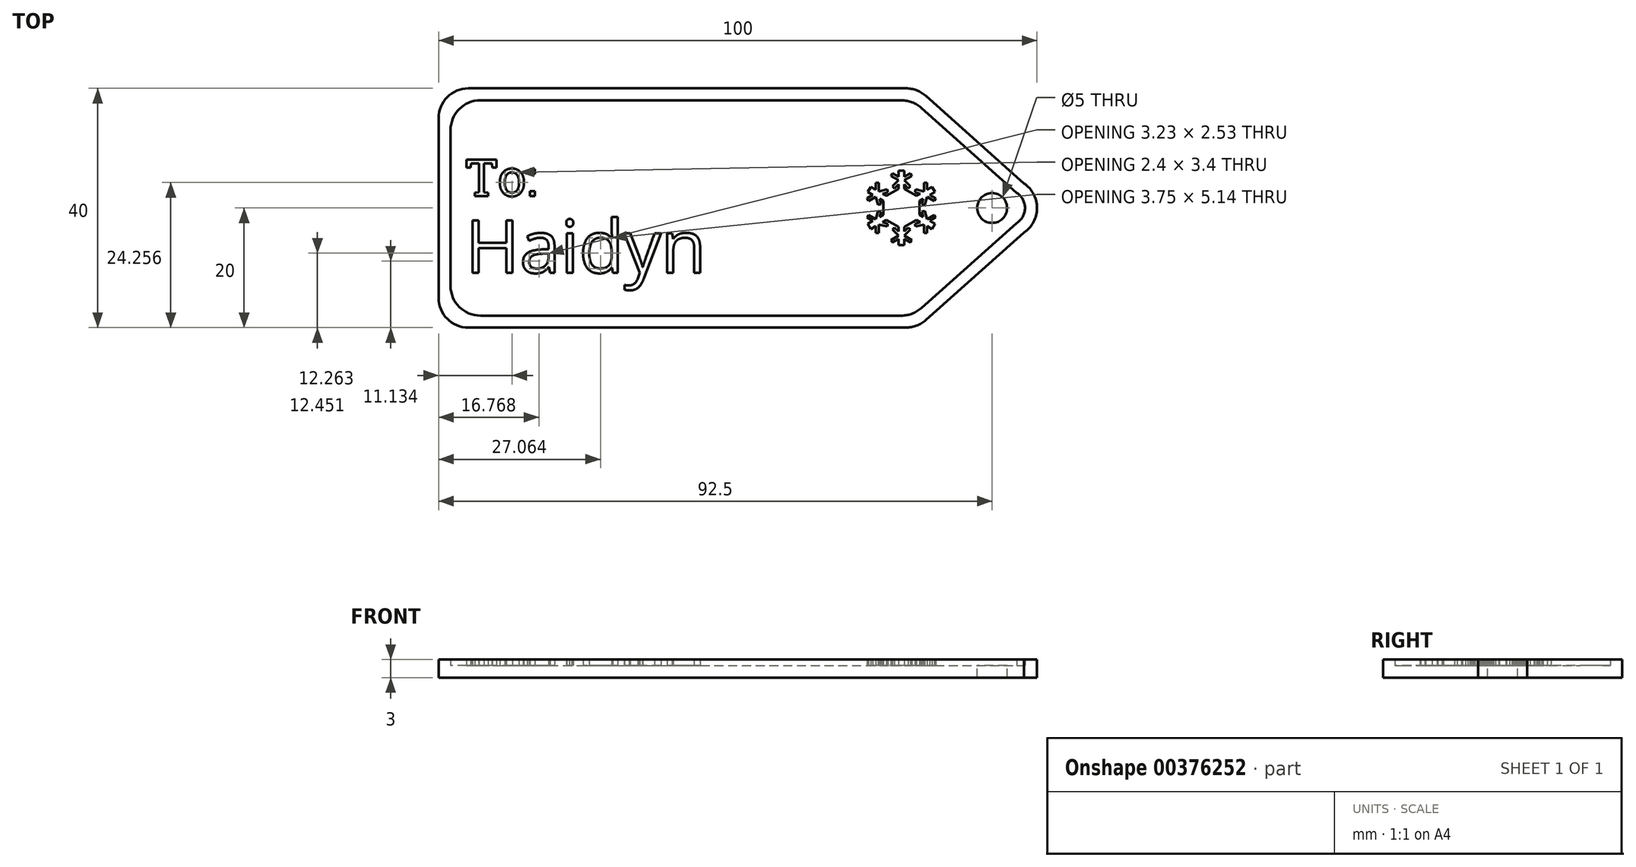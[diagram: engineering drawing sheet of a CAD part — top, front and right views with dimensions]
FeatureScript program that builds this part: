
annotation { "Feature Type Name" : "Feature", "Feature Type Description" : "" }
export const myFeature = defineFeature(function(context is Context, id is Id, definition is map)
    precondition{}
    {
        {
            var Q0;
            Q0=qCreatedBy(makeId("Top.planeOp"),FACE);
            var sketch = newSketch(context, id + "F0", { "sketchPlane" : qUnion([Q0])});
            skLineSegment(sketch, "E0.bottom", {"start": v(0, 0) * mm, "end": v(-40, 0) * mm, "construction": true});
            skLineSegment(sketch, "E0.top", {"start": v(0, 20) * mm, "end": v(-40, 20) * mm});
            skLineSegment(sketch, "E0.left", {"start": v(0, 0) * mm, "end": v(0, 20) * mm, "construction": true});
            skLineSegment(sketch, "E0.right", {"start": v(-40, 0) * mm, "end": v(-40, 20) * mm});
            skLineSegment(sketch, "E1.MirrorCS", {"start": v(40, 0) * mm, "end": v(40, 20) * mm});
            skLineSegment(sketch, "E2.MirrorCS", {"start": v(0, 20) * mm, "end": v(40, 20) * mm});
            skLineSegment(sketch, "E3.MirrorCS", {"start": v(-40, 0) * mm, "end": v(-40, -20) * mm});
            skLineSegment(sketch, "E4.MirrorCS", {"start": v(0, -20) * mm, "end": v(-40, -20) * mm});
            skLineSegment(sketch, "E5.MirrorCS", {"start": v(0, -20) * mm, "end": v(40, -20) * mm});
            skLineSegment(sketch, "E6.MirrorCS", {"start": v(40, 0) * mm, "end": v(40, -20) * mm});
            skLineSegment(sketch, "E7", {"start": v(40, 20) * mm, "end": v(57.85, 4.1) * mm});
            skLineSegment(sketch, "E8.MirrorCS", {"start": v(40, -20) * mm, "end": v(57.85, -4.1) * mm});
            skArc(sketch, "E9.trimOffspring", {"start": v(57.85, -4.1) * mm, "mid": v(60, 0) * mm, "end": v(57.85, 4.1) * mm});
            skSolve(sketch);
        }
        {
            var Q0;
            Q0 = qSketchRegion(id + "F0", true);
            extrude(context, id + "F1", {"entities" : qUnion([Q0]), "depth" : 3 * mm});
        }
        {
            var Q0;
            Q0=makeQuery(id+"F1.opExtrude","CAP_FACE",FACE,{"disambiguationData":[OSD([sQuery(id+"F0.wireOp",EDGE,"E0.top"),sQuery(id+"F0.wireOp",EDGE,"E0.right"),sQuery(id+"F0.wireOp",EDGE,"E2.MirrorCS"),sQuery(id+"F0.wireOp",EDGE,"E3.MirrorCS"),sQuery(id+"F0.wireOp",EDGE,"E4.MirrorCS"),sQuery(id+"F0.wireOp",EDGE,"E5.MirrorCS"),sQuery(id+"F0.wireOp",EDGE,"E7"),sQuery(id+"F0.wireOp",EDGE,"E8.MirrorCS"),sQuery(id+"F0.wireOp",EDGE,"E9.trimOffspring")])],"isStart":false});
            shell(context, id + "F2", {"entities" : qUnion([Q0]), "thickness" : 2 * mm});
        }
        {
            var Q0;
            Q0=makeQuery(id+"F1.opExtrude","SWEPT_EDGE",EDGE,{"disambiguationData":[OSD([sQuery(id+"F0.wireOp",EDGE,"E5.MirrorCS"),sQuery(id+"F0.wireOp",EDGE,"E6.MirrorCS"),sQuery(id+"F0.wireOp",EDGE,"E8.MirrorCS")])]});
            var Q1;
            Q1=makeQuery(id+"F1.opExtrude","SWEPT_EDGE",EDGE,{"disambiguationData":[OSD([sQuery(id+"F0.wireOp",EDGE,"E1.MirrorCS"),sQuery(id+"F0.wireOp",EDGE,"E2.MirrorCS"),sQuery(id+"F0.wireOp",EDGE,"E7")])]});
            var Q2;
            Q2=makeQuery(id+"F1.opExtrude","SWEPT_EDGE",EDGE,{"disambiguationData":[OSD([sQuery(id+"F0.wireOp",EDGE,"E3.MirrorCS"),sQuery(id+"F0.wireOp",EDGE,"E4.MirrorCS")])]});
            var Q3;
            Q3=makeQuery(id+"F1.opExtrude","SWEPT_EDGE",EDGE,{"disambiguationData":[OSD([sQuery(id+"F0.wireOp",EDGE,"E0.top"),sQuery(id+"F0.wireOp",EDGE,"E0.right")])]});
            var Q4;
            Q4=makeQuery(id+"F2.opShell","OFFSET_EDGE",EDGE,{"disambiguationData":[OSD([sQuery(id+"F0.wireOp",EDGE,"E3.MirrorCS"),sQuery(id+"F0.wireOp",EDGE,"E4.MirrorCS")])]});
            var Q5;
            Q5=makeQuery(id+"F2.opShell","OFFSET_EDGE",EDGE,{"disambiguationData":[OSD([sQuery(id+"F0.wireOp",EDGE,"E0.top"),sQuery(id+"F0.wireOp",EDGE,"E0.right")])]});
            var Q6;
            Q6=makeQuery(id+"F2.opShell","OFFSET_EDGE",EDGE,{"disambiguationData":[OSD([sQuery(id+"F0.wireOp",EDGE,"E5.MirrorCS"),sQuery(id+"F0.wireOp",EDGE,"E6.MirrorCS"),sQuery(id+"F0.wireOp",EDGE,"E8.MirrorCS")])]});
            var Q7;
            Q7=makeQuery(id+"F2.opShell","OFFSET_EDGE",EDGE,{"disambiguationData":[OSD([sQuery(id+"F0.wireOp",EDGE,"E1.MirrorCS"),sQuery(id+"F0.wireOp",EDGE,"E2.MirrorCS"),sQuery(id+"F0.wireOp",EDGE,"E7")])]});
            fillet(context, id + "F3", {"entities" : qUnion([Q0, Q1, Q2, Q3, Q4, Q5, Q6, Q7]), "radius" : 5 * mm, "tangentPropagation" : true, "allowEdgeOverflow" : false});
        }
        {
            var Q0;
            Q0=makeQuery(id+"F2.opShell","OFFSET_FACE",FACE,{"disambiguationData":[OSD([sQuery(id+"F0.wireOp",EDGE,"E0.top"),sQuery(id+"F0.wireOp",EDGE,"E0.right"),sQuery(id+"F0.wireOp",EDGE,"E2.MirrorCS"),sQuery(id+"F0.wireOp",EDGE,"E3.MirrorCS"),sQuery(id+"F0.wireOp",EDGE,"E4.MirrorCS"),sQuery(id+"F0.wireOp",EDGE,"E5.MirrorCS"),sQuery(id+"F0.wireOp",EDGE,"E7"),sQuery(id+"F0.wireOp",EDGE,"E8.MirrorCS"),sQuery(id+"F0.wireOp",EDGE,"E9.trimOffspring")])]});
            var sketch = newSketch(context, id + "F4", { "sketchPlane" : qUnion([Q0])});
            skCircle(sketch, "E10", {"center": v(55, 0) * mm, "radius": 2.5 * mm, "construction": true});
            skCircle(sketch, "E11", {"center": v(52.5, 0) * mm, "radius": 2.5 * mm});
            skSolve(sketch);
        }
        {
            var Q0;
            Q0=makeQuery(id+"F4.imprint","IMPRINT",FACE,{"disambiguationData":[TD([[makeQuery(id+"F4.imprint","IMPRINT",EDGE,{"derivedFrom":sQuery(id+"F4.wireOp",EDGE,"E11")}),1.0]])]});
            var Q1;
            Q1=sQuery(id+"F4.wireOp",EDGE,"E11");
            extrude(context, id + "F5", {"entities" : qUnion([Q0]), "operationType" : NewBodyOperationType.REMOVE, "surfaceEntities" : qUnion([Q1]), "endBound" : BoundingType.THROUGH_ALL, "oppositeDirection" : true, "depth" : 25 * mm});
        }
        {
            var Q0;
            Q0=makeQuery(id+"F2.opShell","OFFSET_FACE",FACE,{"disambiguationData":[OSD([sQuery(id+"F0.wireOp",EDGE,"E0.top"),sQuery(id+"F0.wireOp",EDGE,"E0.right"),sQuery(id+"F0.wireOp",EDGE,"E2.MirrorCS"),sQuery(id+"F0.wireOp",EDGE,"E3.MirrorCS"),sQuery(id+"F0.wireOp",EDGE,"E4.MirrorCS"),sQuery(id+"F0.wireOp",EDGE,"E5.MirrorCS"),sQuery(id+"F0.wireOp",EDGE,"E7"),sQuery(id+"F0.wireOp",EDGE,"E8.MirrorCS"),sQuery(id+"F0.wireOp",EDGE,"E9.trimOffspring")])]});
            var sketch = newSketch(context, id + "F6", { "sketchPlane" : qUnion([Q0])});
            skText(sketch, "E12", { "text": "Haidyn", "fontName": "OpenSans-Regular.ttf"});
            skText(sketch, "E13", { "text": "To:", "fontName": "RobotoSlab-Regular.ttf"});
            const initialGuessF6  = {"E12": [-0.0355, -0.01083, 1, 0, 0.00883], "E13": [-0.0355, 0.002, 1, 0, 0.00616]};
            skSetInitialGuess(sketch, initialGuessF6);
            skSolve(sketch);
        }
        {
            var Q0;
            Q0 = qSketchRegion(id + "F6", true);
            extrude(context, id + "F7", {"entities" : qUnion([Q0]), "depth" : 1 * mm});
        }
        {
            var Q0;
            Q0=makeQuery(id+"F2.opShell","OFFSET_FACE",FACE,{"disambiguationData":[OSD([sQuery(id+"F0.wireOp",EDGE,"E0.top"),sQuery(id+"F0.wireOp",EDGE,"E0.right"),sQuery(id+"F0.wireOp",EDGE,"E2.MirrorCS"),sQuery(id+"F0.wireOp",EDGE,"E3.MirrorCS"),sQuery(id+"F0.wireOp",EDGE,"E4.MirrorCS"),sQuery(id+"F0.wireOp",EDGE,"E5.MirrorCS"),sQuery(id+"F0.wireOp",EDGE,"E7"),sQuery(id+"F0.wireOp",EDGE,"E8.MirrorCS"),sQuery(id+"F0.wireOp",EDGE,"E9.trimOffspring")])]});
            var sketch = newSketch(context, id + "F8", { "sketchPlane" : qUnion([Q0])});
            skCircle(sketch, "E14.cCircle", {"center": v(37.34, 0) * mm, "radius": 3 * mm, "construction": true});
            skLineSegment(sketch, "E14.0", {"start": v(40.34, 1.73) * mm, "end": v(40.34, -1.73) * mm});
            skLineSegment(sketch, "E14.1", {"start": v(40.34, -1.73) * mm, "end": v(37.34, -3.46) * mm});
            skLineSegment(sketch, "E14.2", {"start": v(37.34, -3.46) * mm, "end": v(34.34, -1.73) * mm});
            skLineSegment(sketch, "E14.3", {"start": v(34.34, -1.73) * mm, "end": v(34.34, 1.73) * mm});
            skLineSegment(sketch, "E14.4", {"start": v(34.34, 1.73) * mm, "end": v(36.84, 3.18) * mm});
            skLineSegment(sketch, "E14.5", {"start": v(37.34, 3.46) * mm, "end": v(40.34, 1.73) * mm});
            skPoint(sketch, "E14.0.midPoint", {"position": v(40.34, 0) * mm});
            skLineSegment(sketch, "E15", {"start": v(37.34, 18) * mm, "end": v(37.34, -18) * mm, "construction": true});
            skLineSegment(sketch, "E16", {"start": v(37.34, -5.46) * mm, "end": v(37.34, 0) * mm, "construction": true});
            skLineSegment(sketch, "E17.top", {"start": v(37.34, 6.2) * mm, "end": v(36.84, 6.2) * mm});
            skLineSegment(sketch, "E17.left", {"start": v(37.34, 3) * mm, "end": v(37.34, 6.2) * mm});
            skLineSegment(sketch, "E18", {"start": v(36.84, 6.2) * mm, "end": v(36.84, 5.2) * mm});
            skLineSegment(sketch, "E19", {"start": v(36.19, 3.28) * mm, "end": v(35.84, 3.63) * mm});
            skLineSegment(sketch, "E20", {"start": v(36.84, 4.63) * mm, "end": v(35.59, 5.35) * mm});
            skLineSegment(sketch, "E21", {"start": v(35.59, 5.35) * mm, "end": v(35.84, 5.79) * mm});
            skLineSegment(sketch, "E22", {"start": v(35.84, 5.79) * mm, "end": v(36.84, 5.2) * mm});
            skLineSegment(sketch, "E23", {"start": v(36.19, 3.28) * mm, "end": v(36.84, 3.93) * mm});
            skLineSegment(sketch, "E24", {"start": v(35.84, 3.63) * mm, "end": v(36.84, 4.63) * mm});
            skLineSegment(sketch, "E25.trimOffspring", {"start": v(36.84, 3.93) * mm, "end": v(36.84, 3.18) * mm});
            skLineSegment(sketch, "E26.MirrorCS", {"start": v(38.84, 5.79) * mm, "end": v(37.84, 5.2) * mm});
            skLineSegment(sketch, "E27.MirrorCS", {"start": v(39.09, 5.35) * mm, "end": v(38.84, 5.79) * mm});
            skLineSegment(sketch, "E28.MirrorCS", {"start": v(37.84, 6.2) * mm, "end": v(37.84, 5.2) * mm});
            skLineSegment(sketch, "E29.MirrorCS", {"start": v(37.34, 6.2) * mm, "end": v(37.84, 6.2) * mm});
            skLineSegment(sketch, "E30.MirrorCS", {"start": v(37.84, 4.63) * mm, "end": v(39.09, 5.35) * mm});
            skLineSegment(sketch, "E31.MirrorCS", {"start": v(38.84, 3.63) * mm, "end": v(37.84, 4.63) * mm});
            skLineSegment(sketch, "E32.MirrorCS", {"start": v(38.48, 3.28) * mm, "end": v(38.84, 3.63) * mm});
            skLineSegment(sketch, "E33.MirrorCS", {"start": v(38.48, 3.28) * mm, "end": v(37.84, 3.93) * mm});
            skLineSegment(sketch, "E34.MirrorCS", {"start": v(37.84, 3.93) * mm, "end": v(37.84, 3.18) * mm});
            skLineSegment(sketch, "E35.1.0", {"start": v(34.19, 2.4) * mm, "end": v(34.84, 2.02) * mm});
            skLineSegment(sketch, "E35.1.1", {"start": v(35.07, 2.63) * mm, "end": v(34.19, 2.4) * mm});
            skLineSegment(sketch, "E35.1.2", {"start": v(35.07, 2.63) * mm, "end": v(34.94, 3.12) * mm});
            skLineSegment(sketch, "E35.1.3", {"start": v(34.94, 3.12) * mm, "end": v(33.57, 2.75) * mm});
            skLineSegment(sketch, "E35.1.4", {"start": v(33.57, 2.75) * mm, "end": v(33.57, 4.2) * mm});
            skLineSegment(sketch, "E35.1.5", {"start": v(33.57, 4.2) * mm, "end": v(33.07, 4.2) * mm});
            skLineSegment(sketch, "E35.1.6", {"start": v(33.07, 4.2) * mm, "end": v(33.07, 3.04) * mm});
            skLineSegment(sketch, "E35.1.7", {"start": v(32.2, 3.54) * mm, "end": v(33.07, 3.04) * mm});
            skLineSegment(sketch, "E35.1.8", {"start": v(31.96, 3.1) * mm, "end": v(32.2, 3.54) * mm});
            skLineSegment(sketch, "E35.1.9", {"start": v(31.96, 3.1) * mm, "end": v(31.7, 2.67) * mm});
            skLineSegment(sketch, "E35.1.10", {"start": v(31.7, 2.67) * mm, "end": v(32.57, 2.17) * mm});
            skLineSegment(sketch, "E35.1.11", {"start": v(31.57, 1.6) * mm, "end": v(32.57, 2.17) * mm});
            skLineSegment(sketch, "E35.1.12", {"start": v(33.07, 1.88) * mm, "end": v(31.82, 1.16) * mm});
            skLineSegment(sketch, "E35.1.13", {"start": v(31.82, 1.16) * mm, "end": v(31.57, 1.6) * mm});
            skLineSegment(sketch, "E35.1.14", {"start": v(33.44, 0.52) * mm, "end": v(33.07, 1.88) * mm});
            skLineSegment(sketch, "E35.1.15", {"start": v(33.92, 0.65) * mm, "end": v(33.69, 1.53) * mm});
            skLineSegment(sketch, "E35.1.16", {"start": v(33.92, 0.65) * mm, "end": v(33.44, 0.52) * mm});
            skLineSegment(sketch, "E35.1.17", {"start": v(33.69, 1.53) * mm, "end": v(34.34, 1.15) * mm});
            skLineSegment(sketch, "E35.2.0", {"start": v(33.69, -1.53) * mm, "end": v(34.34, -1.15) * mm});
            skLineSegment(sketch, "E35.2.1", {"start": v(33.92, -0.65) * mm, "end": v(33.69, -1.53) * mm});
            skLineSegment(sketch, "E35.2.2", {"start": v(33.92, -0.65) * mm, "end": v(33.44, -0.52) * mm});
            skLineSegment(sketch, "E35.2.3", {"start": v(33.44, -0.52) * mm, "end": v(33.07, -1.88) * mm});
            skLineSegment(sketch, "E35.2.4", {"start": v(33.07, -1.88) * mm, "end": v(31.82, -1.16) * mm});
            skLineSegment(sketch, "E35.2.5", {"start": v(31.82, -1.16) * mm, "end": v(31.57, -1.6) * mm});
            skLineSegment(sketch, "E35.2.6", {"start": v(31.57, -1.6) * mm, "end": v(32.57, -2.17) * mm});
            skLineSegment(sketch, "E35.2.7", {"start": v(31.7, -2.67) * mm, "end": v(32.57, -2.17) * mm});
            skLineSegment(sketch, "E35.2.8", {"start": v(31.96, -3.1) * mm, "end": v(31.7, -2.67) * mm});
            skLineSegment(sketch, "E35.2.9", {"start": v(31.96, -3.1) * mm, "end": v(32.2, -3.54) * mm});
            skLineSegment(sketch, "E35.2.10", {"start": v(32.2, -3.54) * mm, "end": v(33.07, -3.04) * mm});
            skLineSegment(sketch, "E35.2.11", {"start": v(33.07, -4.2) * mm, "end": v(33.07, -3.04) * mm});
            skLineSegment(sketch, "E35.2.12", {"start": v(33.57, -2.75) * mm, "end": v(33.57, -4.2) * mm});
            skLineSegment(sketch, "E35.2.13", {"start": v(33.57, -4.2) * mm, "end": v(33.07, -4.2) * mm});
            skLineSegment(sketch, "E35.2.14", {"start": v(34.94, -3.12) * mm, "end": v(33.57, -2.75) * mm});
            skLineSegment(sketch, "E35.2.15", {"start": v(35.07, -2.63) * mm, "end": v(34.19, -2.4) * mm});
            skLineSegment(sketch, "E35.2.16", {"start": v(35.07, -2.63) * mm, "end": v(34.94, -3.12) * mm});
            skLineSegment(sketch, "E35.2.17", {"start": v(34.19, -2.4) * mm, "end": v(34.84, -2.02) * mm});
            skLineSegment(sketch, "E35.3.0", {"start": v(36.84, -3.93) * mm, "end": v(36.84, -3.18) * mm});
            skLineSegment(sketch, "E35.3.1", {"start": v(36.19, -3.28) * mm, "end": v(36.84, -3.93) * mm});
            skLineSegment(sketch, "E35.3.2", {"start": v(36.19, -3.28) * mm, "end": v(35.84, -3.63) * mm});
            skLineSegment(sketch, "E35.3.3", {"start": v(35.84, -3.63) * mm, "end": v(36.84, -4.63) * mm});
            skLineSegment(sketch, "E35.3.4", {"start": v(36.84, -4.63) * mm, "end": v(35.59, -5.35) * mm});
            skLineSegment(sketch, "E35.3.5", {"start": v(35.59, -5.35) * mm, "end": v(35.84, -5.79) * mm});
            skLineSegment(sketch, "E35.3.6", {"start": v(35.84, -5.79) * mm, "end": v(36.84, -5.2) * mm});
            skLineSegment(sketch, "E35.3.7", {"start": v(36.84, -6.2) * mm, "end": v(36.84, -5.2) * mm});
            skLineSegment(sketch, "E35.3.8", {"start": v(37.34, -6.2) * mm, "end": v(36.84, -6.2) * mm});
            skLineSegment(sketch, "E35.3.9", {"start": v(37.34, -6.2) * mm, "end": v(37.84, -6.2) * mm});
            skLineSegment(sketch, "E35.3.10", {"start": v(37.84, -6.2) * mm, "end": v(37.84, -5.2) * mm});
            skLineSegment(sketch, "E35.3.11", {"start": v(38.84, -5.79) * mm, "end": v(37.84, -5.2) * mm});
            skLineSegment(sketch, "E35.3.12", {"start": v(37.84, -4.63) * mm, "end": v(39.09, -5.35) * mm});
            skLineSegment(sketch, "E35.3.13", {"start": v(39.09, -5.35) * mm, "end": v(38.84, -5.79) * mm});
            skLineSegment(sketch, "E35.3.14", {"start": v(38.84, -3.63) * mm, "end": v(37.84, -4.63) * mm});
            skLineSegment(sketch, "E35.3.15", {"start": v(38.48, -3.28) * mm, "end": v(37.84, -3.93) * mm});
            skLineSegment(sketch, "E35.3.16", {"start": v(38.48, -3.28) * mm, "end": v(38.84, -3.63) * mm});
            skLineSegment(sketch, "E35.3.17", {"start": v(37.84, -3.93) * mm, "end": v(37.84, -3.18) * mm});
            skLineSegment(sketch, "E35.4.0", {"start": v(40.49, -2.4) * mm, "end": v(39.84, -2.02) * mm});
            skLineSegment(sketch, "E35.4.1", {"start": v(39.6, -2.63) * mm, "end": v(40.49, -2.4) * mm});
            skLineSegment(sketch, "E35.4.2", {"start": v(39.6, -2.63) * mm, "end": v(39.73, -3.12) * mm});
            skLineSegment(sketch, "E35.4.3", {"start": v(39.73, -3.12) * mm, "end": v(41.1, -2.75) * mm});
            skLineSegment(sketch, "E35.4.4", {"start": v(41.1, -2.75) * mm, "end": v(41.1, -4.2) * mm});
            skLineSegment(sketch, "E35.4.5", {"start": v(41.1, -4.2) * mm, "end": v(41.6, -4.2) * mm});
            skLineSegment(sketch, "E35.4.6", {"start": v(41.6, -4.2) * mm, "end": v(41.6, -3.04) * mm});
            skLineSegment(sketch, "E35.4.7", {"start": v(42.46, -3.54) * mm, "end": v(41.6, -3.04) * mm});
            skLineSegment(sketch, "E35.4.8", {"start": v(42.71, -3.1) * mm, "end": v(42.46, -3.54) * mm});
            skLineSegment(sketch, "E35.4.9", {"start": v(42.71, -3.1) * mm, "end": v(42.96, -2.67) * mm});
            skLineSegment(sketch, "E35.4.10", {"start": v(42.96, -2.67) * mm, "end": v(42.1, -2.17) * mm});
            skLineSegment(sketch, "E35.4.11", {"start": v(43.1, -1.6) * mm, "end": v(42.1, -2.17) * mm});
            skLineSegment(sketch, "E35.4.12", {"start": v(41.6, -1.88) * mm, "end": v(42.85, -1.16) * mm});
            skLineSegment(sketch, "E35.4.13", {"start": v(42.85, -1.16) * mm, "end": v(43.1, -1.6) * mm});
            skLineSegment(sketch, "E35.4.14", {"start": v(41.23, -0.52) * mm, "end": v(41.6, -1.88) * mm});
            skLineSegment(sketch, "E35.4.15", {"start": v(40.75, -0.65) * mm, "end": v(40.99, -1.53) * mm});
            skLineSegment(sketch, "E35.4.16", {"start": v(40.75, -0.65) * mm, "end": v(41.23, -0.52) * mm});
            skLineSegment(sketch, "E35.4.17", {"start": v(40.99, -1.53) * mm, "end": v(40.34, -1.15) * mm});
            skLineSegment(sketch, "E35.5.0", {"start": v(40.99, 1.53) * mm, "end": v(40.34, 1.15) * mm});
            skLineSegment(sketch, "E35.5.1", {"start": v(40.75, 0.65) * mm, "end": v(40.99, 1.53) * mm});
            skLineSegment(sketch, "E35.5.2", {"start": v(40.75, 0.65) * mm, "end": v(41.23, 0.52) * mm});
            skLineSegment(sketch, "E35.5.3", {"start": v(41.23, 0.52) * mm, "end": v(41.6, 1.88) * mm});
            skLineSegment(sketch, "E35.5.4", {"start": v(41.6, 1.88) * mm, "end": v(42.85, 1.16) * mm});
            skLineSegment(sketch, "E35.5.5", {"start": v(42.85, 1.16) * mm, "end": v(43.1, 1.6) * mm});
            skLineSegment(sketch, "E35.5.6", {"start": v(43.1, 1.6) * mm, "end": v(42.1, 2.17) * mm});
            skLineSegment(sketch, "E35.5.7", {"start": v(42.96, 2.67) * mm, "end": v(42.1, 2.17) * mm});
            skLineSegment(sketch, "E35.5.8", {"start": v(42.71, 3.1) * mm, "end": v(42.96, 2.67) * mm});
            skLineSegment(sketch, "E35.5.9", {"start": v(42.71, 3.1) * mm, "end": v(42.46, 3.54) * mm});
            skLineSegment(sketch, "E35.5.10", {"start": v(42.46, 3.54) * mm, "end": v(41.6, 3.04) * mm});
            skLineSegment(sketch, "E35.5.11", {"start": v(41.6, 4.2) * mm, "end": v(41.6, 3.04) * mm});
            skLineSegment(sketch, "E35.5.12", {"start": v(41.1, 2.75) * mm, "end": v(41.1, 4.2) * mm});
            skLineSegment(sketch, "E35.5.13", {"start": v(41.1, 4.2) * mm, "end": v(41.6, 4.2) * mm});
            skLineSegment(sketch, "E35.5.14", {"start": v(39.73, 3.12) * mm, "end": v(41.1, 2.75) * mm});
            skLineSegment(sketch, "E35.5.15", {"start": v(39.6, 2.63) * mm, "end": v(40.49, 2.4) * mm});
            skLineSegment(sketch, "E35.5.16", {"start": v(39.6, 2.63) * mm, "end": v(39.73, 3.12) * mm});
            skLineSegment(sketch, "E35.5.17", {"start": v(40.49, 2.4) * mm, "end": v(39.84, 2.02) * mm});
            skSolve(sketch);
        }
        {
            var Q0;
            Q0 = qSketchRegion(id + "F8", true);
            extrude(context, id + "F9", {"entities" : qUnion([Q0]), "operationType" : NewBodyOperationType.ADD, "depth" : 1 * mm});
        }
    });
